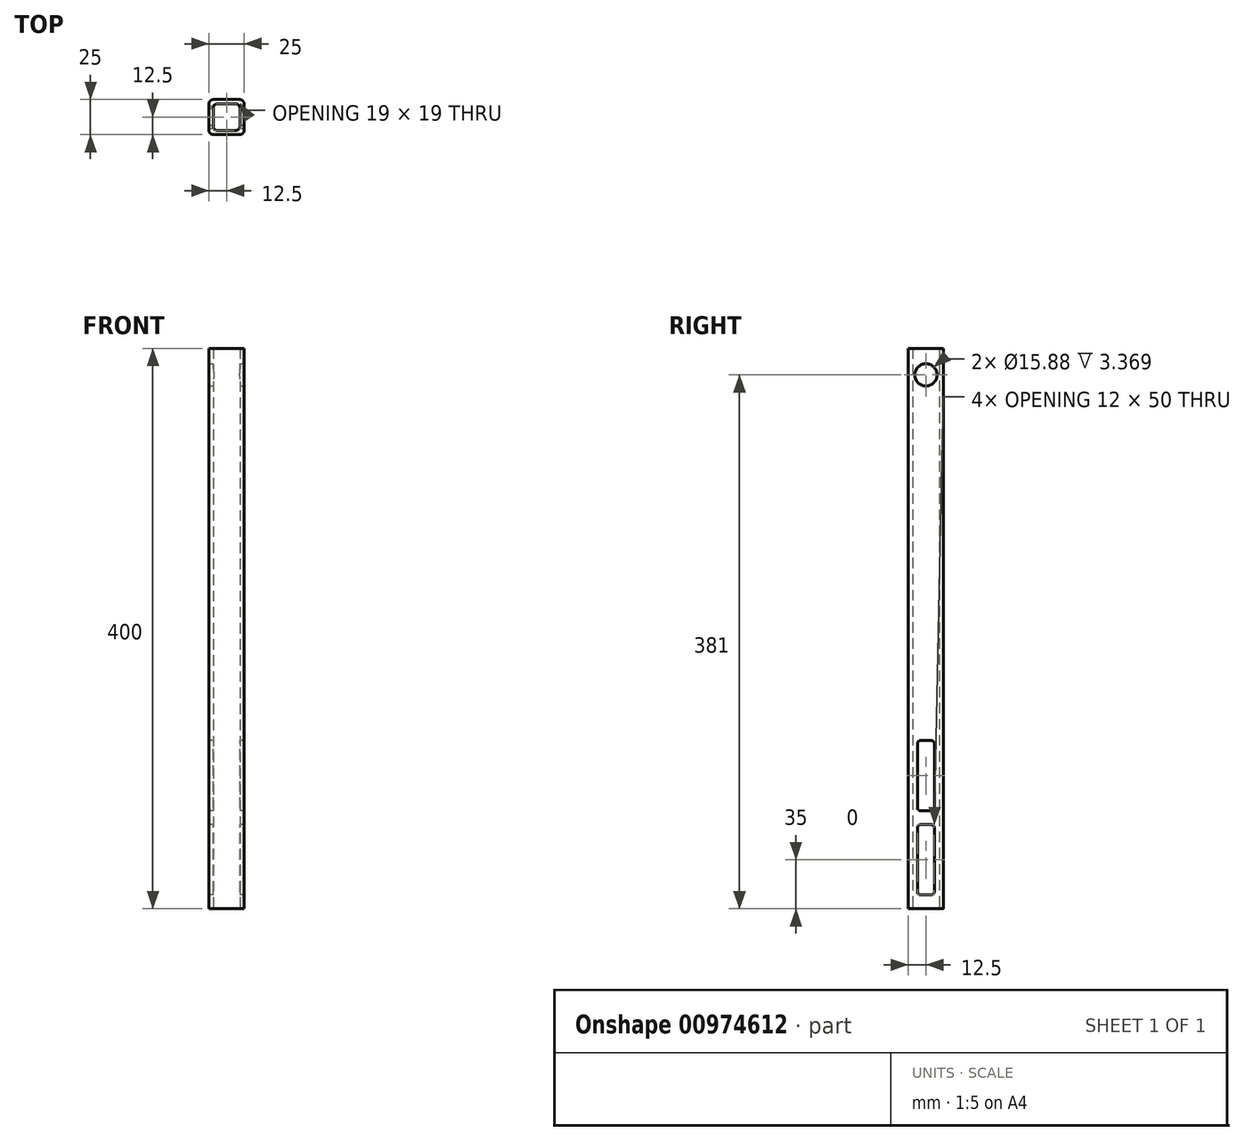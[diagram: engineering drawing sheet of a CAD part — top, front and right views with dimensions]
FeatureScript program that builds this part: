
annotation { "Feature Type Name" : "Feature", "Feature Type Description" : "" }
export const myFeature = defineFeature(function(context is Context, id is Id, definition is map)
    precondition{}
    {
        {
            var Q0;
            Q0=qCreatedBy(makeId("Top.planeOp"),FACE);
            var sketch = newSketch(context, id + "F0", { "sketchPlane" : qUnion([Q0])});
            skLineSegment(sketch, "E0.bottom", {"start": v(9.5, 12.5) * mm, "end": v(-9.5, 12.5) * mm});
            skLineSegment(sketch, "E0.top", {"start": v(9.5, -12.5) * mm, "end": v(-9.5, -12.5) * mm});
            skLineSegment(sketch, "E0.left", {"start": v(12.5, 9.5) * mm, "end": v(12.5, -9.5) * mm});
            skLineSegment(sketch, "E0.right", {"start": v(-12.5, 9.5) * mm, "end": v(-12.5, -9.5) * mm});
            skPoint(sketch, "E0.middle", {"position": v(0, 0) * mm});
            skLineSegment(sketch, "E1.0", {"start": v(6.5, 9.5) * mm, "end": v(-6.5, 9.5) * mm});
            skLineSegment(sketch, "E1.1", {"start": v(9.5, 6.5) * mm, "end": v(9.5, -6.5) * mm});
            skLineSegment(sketch, "E1.2", {"start": v(6.5, -9.5) * mm, "end": v(-6.5, -9.5) * mm});
            skLineSegment(sketch, "E1.3", {"start": v(-9.5, 6.5) * mm, "end": v(-9.5, -6.5) * mm});
            skPoint(sketch, "E2.visualSharp", {"position": v(-12.5, 12.5) * mm});
            skArc(sketch, "E2.filletArc", {"start": v(-9.5, 12.5) * mm, "mid": v(-11.62, 11.62) * mm, "end": v(-12.5, 9.5) * mm});
            skArc(sketch, "E3.filletArc", {"start": v(-6.5, 9.5) * mm, "mid": v(-8.62, 8.62) * mm, "end": v(-9.5, 6.5) * mm});
            skPoint(sketch, "E4.visualSharp", {"position": v(-9.5, -9.5) * mm});
            skArc(sketch, "E4.filletArc", {"start": v(-9.5, -6.5) * mm, "mid": v(-8.62, -8.62) * mm, "end": v(-6.5, -9.5) * mm});
            skPoint(sketch, "E5.visualSharp", {"position": v(12.5, -12.5) * mm});
            skArc(sketch, "E5.filletArc", {"start": v(9.5, -12.5) * mm, "mid": v(11.62, -11.62) * mm, "end": v(12.5, -9.5) * mm});
            skArc(sketch, "E6.filletArc", {"start": v(6.5, -9.5) * mm, "mid": v(8.62, -8.62) * mm, "end": v(9.5, -6.5) * mm});
            skPoint(sketch, "E7.visualSharp", {"position": v(-12.5, -12.5) * mm});
            skArc(sketch, "E7.filletArc", {"start": v(-12.5, -9.5) * mm, "mid": v(-11.62, -11.62) * mm, "end": v(-9.5, -12.5) * mm});
            skPoint(sketch, "E8.visualSharp", {"position": v(12.5, 12.5) * mm});
            skArc(sketch, "E8.filletArc", {"start": v(12.5, 9.5) * mm, "mid": v(11.62, 11.62) * mm, "end": v(9.5, 12.5) * mm});
            skArc(sketch, "E9.filletArc", {"start": v(9.5, 6.5) * mm, "mid": v(8.62, 8.62) * mm, "end": v(6.5, 9.5) * mm});
            skSolve(sketch);
        }
        {
            var Q0;
            Q0 = qSketchRegion(id + "F0", true);
            extrude(context, id + "F1", {"entities" : qUnion([Q0]), "depth" : 400 * mm, "offsetDistance" : 25 * mm});
        }
        {
            var Q0;
            Q0=makeQuery(id+"F1.opExtrude","SWEPT_FACE",FACE,{"disambiguationData":[OSD([sQuery(id+"F0.wireOp",EDGE,"E0.right")])]});
            var sketch = newSketch(context, id + "F2", { "sketchPlane" : qUnion([Q0])});
            skLineSegment(sketch, "E10", {"start": v(0, 0) * mm, "end": v(0, 413.17) * mm, "construction": true});
            skLineSegment(sketch, "E11.bottom", {"start": v(4, 60) * mm, "end": v(-4, 60) * mm});
            skLineSegment(sketch, "E11.top", {"start": v(4, 10) * mm, "end": v(-4, 10) * mm});
            skLineSegment(sketch, "E11.left", {"start": v(6, 58) * mm, "end": v(6, 12) * mm});
            skLineSegment(sketch, "E11.right", {"start": v(-6, 58) * mm, "end": v(-6, 12) * mm});
            skPoint(sketch, "E11.middle", {"position": v(0, 35) * mm});
            skLineSegment(sketch, "E12.bottom", {"start": v(4, 120) * mm, "end": v(-4, 120) * mm});
            skLineSegment(sketch, "E12.top", {"start": v(4, 70) * mm, "end": v(-4, 70) * mm});
            skLineSegment(sketch, "E12.left", {"start": v(6, 118) * mm, "end": v(6, 72) * mm});
            skLineSegment(sketch, "E12.right", {"start": v(-6, 118) * mm, "end": v(-6, 72) * mm});
            skPoint(sketch, "E12.middle", {"position": v(0, 95) * mm});
            skPoint(sketch, "E13.visualSharp", {"position": v(-6, 120) * mm});
            skArc(sketch, "E13.filletArc", {"start": v(-4, 120) * mm, "mid": v(-5.41, 119.41) * mm, "end": v(-6, 118) * mm});
            skPoint(sketch, "E14.visualSharp", {"position": v(6, 120) * mm});
            skArc(sketch, "E14.filletArc", {"start": v(6, 118) * mm, "mid": v(5.41, 119.41) * mm, "end": v(4, 120) * mm});
            skPoint(sketch, "E15.visualSharp", {"position": v(6, 70) * mm});
            skArc(sketch, "E15.filletArc", {"start": v(4, 70) * mm, "mid": v(5.41, 70.59) * mm, "end": v(6, 72) * mm});
            skPoint(sketch, "E16.visualSharp", {"position": v(-6, 70) * mm});
            skArc(sketch, "E16.filletArc", {"start": v(-6, 72) * mm, "mid": v(-5.41, 70.59) * mm, "end": v(-4, 70) * mm});
            skPoint(sketch, "E17.visualSharp", {"position": v(-6, 60) * mm});
            skArc(sketch, "E17.filletArc", {"start": v(-4, 60) * mm, "mid": v(-5.41, 59.41) * mm, "end": v(-6, 58) * mm});
            skPoint(sketch, "E18.visualSharp", {"position": v(-6, 10) * mm});
            skArc(sketch, "E18.filletArc", {"start": v(-6, 12) * mm, "mid": v(-5.41, 10.59) * mm, "end": v(-4, 10) * mm});
            skPoint(sketch, "E19.visualSharp", {"position": v(6, 60) * mm});
            skArc(sketch, "E19.filletArc", {"start": v(6, 58) * mm, "mid": v(5.41, 59.41) * mm, "end": v(4, 60) * mm});
            skPoint(sketch, "E20.visualSharp", {"position": v(6, 10) * mm});
            skArc(sketch, "E20.filletArc", {"start": v(4, 10) * mm, "mid": v(5.41, 10.59) * mm, "end": v(6, 12) * mm});
            skSolve(sketch);
        }
        {
            var Q0;
            Q0 = qSketchRegion(id + "F2", true);
            extrude(context, id + "F3", {"entities" : qUnion([Q0]), "operationType" : NewBodyOperationType.REMOVE, "endBound" : BoundingType.THROUGH_ALL, "oppositeDirection" : true, "depth" : 25 * mm, "offsetDistance" : 25 * mm});
        }
        {
            var Q0;
            Q0=makeQuery(id+"F1.opExtrude","SWEPT_FACE",FACE,{"disambiguationData":[OSD([sQuery(id+"F0.wireOp",EDGE,"E0.left")])]});
            var sketch = newSketch(context, id + "F4", { "sketchPlane" : qUnion([Q0])});
            skCircle(sketch, "E21", {"center": v(0, 381) * mm, "radius": 7.94 * mm});
            skSolve(sketch);
        }
        {
            var Q0;
            Q0 = qSketchRegion(id + "F4", true);
            extrude(context, id + "F5", {"entities" : qUnion([Q0]), "operationType" : NewBodyOperationType.REMOVE, "endBound" : BoundingType.THROUGH_ALL, "oppositeDirection" : true, "depth" : 25 * mm, "offsetDistance" : 25 * mm});
        }
    });
